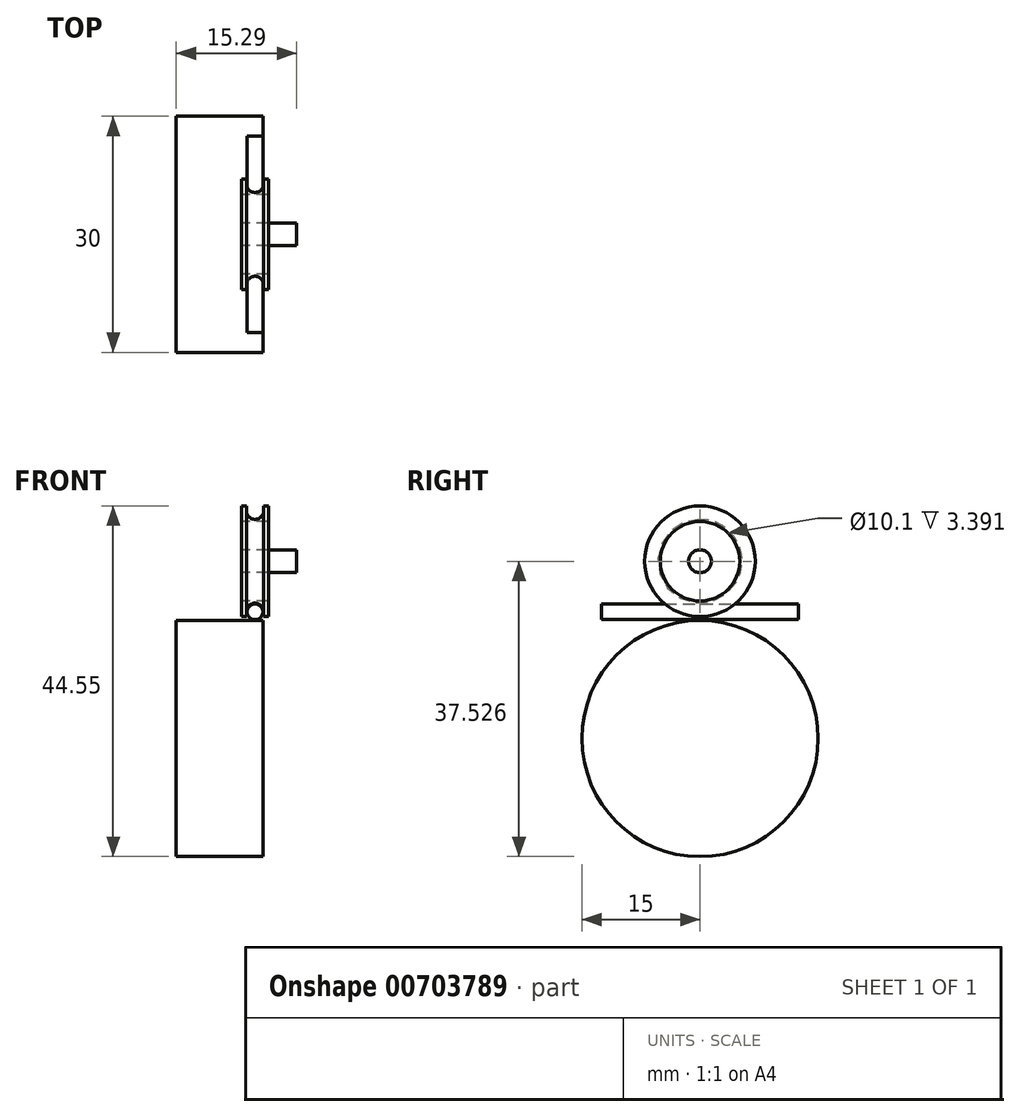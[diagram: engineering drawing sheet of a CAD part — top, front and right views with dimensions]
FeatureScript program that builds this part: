
annotation { "Feature Type Name" : "Feature", "Feature Type Description" : "" }
export const myFeature = defineFeature(function(context is Context, id is Id, definition is map)
    precondition{}
    {
        {
            var Q0;
            Q0=qCreatedBy(makeId("Front.planeOp"),FACE);
            var sketch = newSketch(context, id + "F0", { "sketchPlane" : qUnion([Q0])});
            skCircle(sketch, "E0", {"center": v(0, 0) * mm, "radius": 1 * mm, "construction": true});
            skLineSegment(sketch, "E1", {"start": v(0, 1) * mm, "end": v(4.5, 1) * mm, "construction": true});
            skLineSegment(sketch, "E2", {"start": v(0, -1) * mm, "end": v(4.5, -1) * mm, "construction": true});
            skLineSegment(sketch, "E3", {"start": v(0, 0) * mm, "end": v(4.5, 0) * mm, "construction": true});
            skCircle(sketch, "E4", {"center": v(4.5, 0) * mm, "radius": 1 * mm, "construction": true});
            skCircle(sketch, "E5.MirrorC", {"center": v(-4.5, 0) * mm, "radius": 1 * mm, "construction": true});
            skLineSegment(sketch, "E6.MirrorCS", {"start": v(0, 0) * mm, "end": v(-4.5, 0) * mm, "construction": true});
            skLineSegment(sketch, "E7.MirrorCS", {"start": v(0, -1) * mm, "end": v(-4.5, -1) * mm, "construction": true});
            skLineSegment(sketch, "E8.MirrorCS", {"start": v(0, 1) * mm, "end": v(-4.5, 1) * mm, "construction": true});
            skLineSegment(sketch, "E9", {"start": v(1, 0) * mm, "end": v(1, 10.9) * mm, "construction": true});
            skLineSegment(sketch, "E10", {"start": v(-1, 0) * mm, "end": v(-1, 10.9) * mm, "construction": true});
            skPoint(sketch, "E11", {"position": v(-5.5, 0) * mm});
            skPoint(sketch, "E12", {"position": v(5.5, 0) * mm});
            skPoint(sketch, "E13", {"position": v(-3.5, 0) * mm});
            skPoint(sketch, "E14", {"position": v(3.5, 0) * mm});
            skLineSegment(sketch, "E15.bottom", {"start": v(-5.33, -38) * mm, "end": v(-40.33, -38) * mm});
            skLineSegment(sketch, "E15.top", {"start": v(-5.33, -28.5) * mm, "end": v(-40.33, -28.5) * mm});
            skLineSegment(sketch, "E15.left", {"start": v(-5.33, -38) * mm, "end": v(-5.33, -28.5) * mm});
            skLineSegment(sketch, "E15.right", {"start": v(-40.33, -38) * mm, "end": v(-40.33, -28.5) * mm});
            skPoint(sketch, "E15.middle", {"position": v(-22.83, -33.26) * mm});
            skSolve(sketch);
        }
        {
            var Q0;
            Q0=qCreatedBy(makeId("Front.planeOp"),FACE);
            var sketch = newSketch(context, id + "F1", { "sketchPlane" : qUnion([Q0])});
            skCircle(sketch, "E16.0", {"center": v(-4.5, 0) * mm, "radius": 1 * mm, "construction": true});
            skCircle(sketch, "E16.1", {"center": v(0, 0) * mm, "radius": 1 * mm, "construction": true});
            skCircle(sketch, "E16.2", {"center": v(4.5, 0) * mm, "radius": 1 * mm, "construction": true});
            skLineSegment(sketch, "E16.3", {"start": v(0, 1) * mm, "end": v(4.5, 1) * mm, "construction": true});
            skLineSegment(sketch, "E16.4", {"start": v(0, -1) * mm, "end": v(4.5, -1) * mm, "construction": true});
            skLineSegment(sketch, "E16.5", {"start": v(0, -1) * mm, "end": v(-4.5, -1) * mm, "construction": true});
            skLineSegment(sketch, "E16.6", {"start": v(0, 1) * mm, "end": v(-4.5, 1) * mm, "construction": true});
            skLineSegment(sketch, "E16.7", {"start": v(1, 0) * mm, "end": v(1, 10.9) * mm, "construction": true});
            skLineSegment(sketch, "E16.8", {"start": v(-1, 0) * mm, "end": v(-1, 10.9) * mm, "construction": true});
            skLineSegment(sketch, "E17.bottom", {"start": v(-5.5, -1.1) * mm, "end": v(5.5, -1.1) * mm});
            skLineSegment(sketch, "E17.top", {"start": v(-5.5, -31.1) * mm, "end": v(5.5, -31.1) * mm});
            skLineSegment(sketch, "E17.left", {"start": v(-5.5, -1.1) * mm, "end": v(-5.5, -31.1) * mm});
            skLineSegment(sketch, "E17.right", {"start": v(5.5, -1.1) * mm, "end": v(5.5, -31.1) * mm});
            skPoint(sketch, "E17.middle", {"position": v(0, -16.1) * mm});
            skLineSegment(sketch, "E18.bottom", {"start": v(2.8, -0.6) * mm, "end": v(6.2, -0.6) * mm});
            skCircle(sketch, "E19.0", {"center": v(4.5, 0) * mm, "radius": 1.1 * mm});
            skLineSegment(sketch, "E20", {"start": v(3.4, 0) * mm, "end": v(3.4, -0.6) * mm});
            skLineSegment(sketch, "E21", {"start": v(5.6, 0) * mm, "end": v(5.6, -0.6) * mm});
            skLineSegment(sketch, "E22", {"start": v(2.8, 6.43) * mm, "end": v(6.2, 6.43) * mm});
            skLineSegment(sketch, "E23", {"start": v(6.2, -0.6) * mm, "end": v(6.2, 6.43) * mm});
            skLineSegment(sketch, "E24", {"start": v(2.8, -0.6) * mm, "end": v(2.8, 6.43) * mm});
            skLineSegment(sketch, "E25", {"start": v(4.5, 1.1) * mm, "end": v(4.5, 1.38) * mm, "construction": true});
            skLineSegment(sketch, "E26", {"start": v(4.5, 1.38) * mm, "end": v(2.8, 1.38) * mm});
            skLineSegment(sketch, "E27", {"start": v(4.5, 1.38) * mm, "end": v(6.2, 1.38) * mm});
            skLineSegment(sketch, "E28", {"start": v(2.8, 4.98) * mm, "end": v(6.2, 4.98) * mm});
            skLineSegment(sketch, "E29", {"start": v(6.2, 4.98) * mm, "end": v(9.79, 4.98) * mm});
            skLineSegment(sketch, "E30", {"start": v(6.2, 6.43) * mm, "end": v(9.79, 6.43) * mm});
            skLineSegment(sketch, "E31", {"start": v(9.79, 6.43) * mm, "end": v(9.79, 4.98) * mm});
            skLineSegment(sketch, "E32", {"start": v(-5.5, -16.1) * mm, "end": v(5.5, -16.1) * mm});
            skPoint(sketch, "E33.middle", {"position": v(5.5, -16.1) * mm});
            skLineSegment(sketch, "E34", {"start": v(6.2, 6.43) * mm, "end": v(6.2, 7.88) * mm});
            skLineSegment(sketch, "E35", {"start": v(6.2, 7.88) * mm, "end": v(9.79, 7.88) * mm});
            skLineSegment(sketch, "E36", {"start": v(9.79, 7.88) * mm, "end": v(9.79, 6.43) * mm});
            skLineSegment(sketch, "E37", {"start": v(6.8, 4.98) * mm, "end": v(6.8, -1.17) * mm});
            skLineSegment(sketch, "E38", {"start": v(9.79, 4.98) * mm, "end": v(9.79, -6.04) * mm});
            skLineSegment(sketch, "E39", {"start": v(5.6, 0) * mm, "end": v(6.2, 0) * mm, "construction": true});
            skLineSegment(sketch, "E40", {"start": v(3.4, 0) * mm, "end": v(2.8, 0) * mm, "construction": true});
            skLineSegment(sketch, "E41", {"start": v(5.5, -16.1) * mm, "end": v(6.5, -16.1) * mm});
            skLineSegment(sketch, "E42", {"start": v(6.5, -16.1) * mm, "end": v(12.2, -16.1) * mm});
            skLineSegment(sketch, "E43", {"start": v(12.2, -16.1) * mm, "end": v(12.2, -24.45) * mm});
            skLineSegment(sketch, "E44.MirrorCS", {"start": v(12.2, -16.1) * mm, "end": v(12.2, -7.75) * mm});
            skLineSegment(sketch, "E45", {"start": v(12.2, -7.75) * mm, "end": v(6.5, -7.75) * mm});
            skLineSegment(sketch, "E46", {"start": v(6.5, -7.75) * mm, "end": v(6.5, -16.1) * mm});
            skLineSegment(sketch, "E47", {"start": v(6.5, -16.1) * mm, "end": v(6.5, -24.45) * mm});
            skLineSegment(sketch, "E48", {"start": v(12.2, -24.45) * mm, "end": v(6.5, -24.45) * mm});
            skSolve(sketch);
        }
        {
            var Q0;
            Q0=qCreatedBy(makeId("Front.planeOp"),FACE);
            var sketch = newSketch(context, id + "F2", { "sketchPlane" : qUnion([Q0])});
            skCircle(sketch, "E49.0", {"center": v(-4.5, 0) * mm, "radius": 1 * mm});
            skCircle(sketch, "E49.1", {"center": v(4.5, 0) * mm, "radius": 1 * mm});
            skLineSegment(sketch, "E50", {"start": v(-4.5, -1) * mm, "end": v(4.5, -1) * mm, "construction": true});
            skLineSegment(sketch, "E51", {"start": v(4.5, -1) * mm, "end": v(6.6, -1) * mm, "construction": true});
            skLineSegment(sketch, "E52", {"start": v(-3.9, -1) * mm, "end": v(-4.5, -1) * mm, "construction": true});
            skLineSegment(sketch, "E53", {"start": v(-4.5, 1) * mm, "end": v(-4.5, -1) * mm, "construction": true});
            skLineSegment(sketch, "E54", {"start": v(-3.9, -1) * mm, "end": v(-3.9, -3) * mm, "construction": true});
            skLineSegment(sketch, "E55", {"start": v(-3.9, -3) * mm, "end": v(6.6, -3) * mm, "construction": true});
            skLineSegment(sketch, "E56", {"start": v(6.6, -3) * mm, "end": v(6.6, -1) * mm, "construction": true});
            skLineSegment(sketch, "E57", {"start": v(-4.68, 1.66) * mm, "end": v(-4.68, -0.66) * mm});
            skLineSegment(sketch, "E58", {"start": v(-4.68, -0.66) * mm, "end": v(-5.18, -0.66) * mm});
            skLineSegment(sketch, "E59", {"start": v(-5.18, -0.66) * mm, "end": v(-5.18, 2) * mm});
            skLineSegment(sketch, "E60", {"start": v(-2.68, 1.66) * mm, "end": v(-2.68, -0.66) * mm});
            skLineSegment(sketch, "E61", {"start": v(-2.68, -0.66) * mm, "end": v(-2.18, -0.66) * mm});
            skLineSegment(sketch, "E62", {"start": v(-2.18, -0.66) * mm, "end": v(-2.18, 2) * mm});
            skLineSegment(sketch, "E63", {"start": v(-5.5, 0) * mm, "end": v(-4.68, 0) * mm, "construction": true});
            skLineSegment(sketch, "E64", {"start": v(-2.68, 0) * mm, "end": v(-3.5, 0) * mm, "construction": true});
            skLineSegment(sketch, "E65", {"start": v(-4.68, -0.66) * mm, "end": v(-2.68, -0.66) * mm, "construction": true});
            skLineSegment(sketch, "E66.bottom", {"start": v(2.82, -0.72) * mm, "end": v(6.18, -0.72) * mm});
            skLineSegment(sketch, "E66.top", {"start": v(2.82, 1.74) * mm, "end": v(6.18, 1.74) * mm});
            skLineSegment(sketch, "E66.left", {"start": v(2.82, -0.72) * mm, "end": v(2.82, 1.74) * mm});
            skLineSegment(sketch, "E66.right", {"start": v(6.18, -0.72) * mm, "end": v(6.18, 1.74) * mm});
            skPoint(sketch, "E66.middle", {"position": v(4.5, 0.5) * mm});
            skLineSegment(sketch, "E67", {"start": v(3.5, 0) * mm, "end": v(3.5, -0.72) * mm});
            skLineSegment(sketch, "E68", {"start": v(5.5, 0) * mm, "end": v(5.5, -0.72) * mm});
            skLineSegment(sketch, "E69", {"start": v(1.38, 2.12) * mm, "end": v(5.95, 2.12) * mm, "construction": true});
            skCircle(sketch, "E70.0", {"center": v(4.5, 0) * mm, "radius": 1.1 * mm});
            skLineSegment(sketch, "E71", {"start": v(5.6, 0) * mm, "end": v(5.6, -0.72) * mm});
            skLineSegment(sketch, "E72", {"start": v(3.4, 0) * mm, "end": v(3.4, -0.72) * mm});
            skLineSegment(sketch, "E73.bottom", {"start": v(6.18, 1.74) * mm, "end": v(0, 1.74) * mm});
            skLineSegment(sketch, "E73.top", {"start": v(6.18, 2.12) * mm, "end": v(0, 2.12) * mm});
            skLineSegment(sketch, "E73.left", {"start": v(6.18, 1.74) * mm, "end": v(6.18, 2.12) * mm});
            skLineSegment(sketch, "E73.right", {"start": v(0, 1.74) * mm, "end": v(0, 2.12) * mm});
            skLineSegment(sketch, "E74.bottom", {"start": v(-1.22, 39.38) * mm, "end": v(8.78, 39.38) * mm});
            skLineSegment(sketch, "E74.top", {"start": v(-1.22, 13.38) * mm, "end": v(8.78, 13.38) * mm});
            skLineSegment(sketch, "E74.left", {"start": v(-1.22, 39.38) * mm, "end": v(-1.22, 13.38) * mm});
            skLineSegment(sketch, "E74.right", {"start": v(8.78, 39.38) * mm, "end": v(8.78, 13.38) * mm});
            skLineSegment(sketch, "E75.bottom", {"start": v(2.28, 3.38) * mm, "end": v(5.28, 3.38) * mm});
            skLineSegment(sketch, "E75.top", {"start": v(2.28, 23.38) * mm, "end": v(5.28, 23.38) * mm});
            skLineSegment(sketch, "E75.left", {"start": v(2.28, 3.38) * mm, "end": v(2.28, 23.38) * mm});
            skLineSegment(sketch, "E75.right", {"start": v(5.28, 3.38) * mm, "end": v(5.28, 23.38) * mm});
            skPoint(sketch, "E75.middle", {"position": v(3.78, 13.38) * mm});
            skSolve(sketch);
        }
        {
            var Q0;
            {var subQ0=sQuery(id+"F2.wireOp",EDGE,"E49.1");var subQ1=makeQuery(id+"F2.imprint","INTERSECT",VERTEX,{"derivedFrom":[subQ0,sQuery(id+"F2.wireOp",EDGE,"E67")]});Q0=makeQuery(id+"F2.imprint","IMPRINT",FACE,{"disambiguationData":[TD([[makeQuery(id+"F2.imprint","IMPRINT",EDGE,{"disambiguationData":[TD([[subQ1,1.0]])],"derivedFrom":subQ0}),1.0]])]});}
            var Q1;
            Q1=makeQuery(id+"F2.imprint","IMPRINT",FACE,{"disambiguationData":[TD([[makeQuery(id+"F2.imprint","IMPRINT",EDGE,{"derivedFrom":sQuery(id+"F2.wireOp",EDGE,"E49.0")}),-1.0]])]});
            var Q2;
            {var subQ0=sQuery(id+"F2.wireOp",EDGE,"E66.bottom");var subQ1=sQuery(id+"F2.wireOp",EDGE,"E49.1");var subQ2=makeQuery(id+"F2.imprint","INTERSECT",VERTEX,{"disambiguationData":[OD(0.0)],"derivedFrom":[subQ1,subQ0]});Q2=makeQuery(id+"F2.imprint","IMPRINT",FACE,{"disambiguationData":[TD([[makeQuery(id+"F2.imprint","IMPRINT",EDGE,{"disambiguationData":[TD([[subQ2,-1.0]])],"derivedFrom":subQ1}),1.0]])]});}
            extrude(context, id + "F3", {"entities" : qUnion([Q0, Q1, Q2]), "endBound" : BoundingType.SYMMETRIC, "depth" : 25 * mm, "offsetDistance" : 25 * mm});
        }
        {
            var Q0;
            {var subQ4=sQuery(id+"F1.wireOp",EDGE,"E20");Q0=makeQuery(id+"F1.imprint","IMPRINT",FACE,{"disambiguationData":[TD([[makeQuery(id+"F1.imprint","IMPRINT",EDGE,{"derivedFrom":subQ4}),-1.0]])]});}
            var Q1;
            {var subQ0=sQuery(id+"F1.wireOp",EDGE,"E22");Q1=makeQuery(id+"F1.imprint","IMPRINT",FACE,{"disambiguationData":[TD([[makeQuery(id+"F1.imprint","IMPRINT",EDGE,{"derivedFrom":subQ0}),-1.0]])]});}
            var Q2;
            {var subQ2=sQuery(id+"F1.wireOp",EDGE,"E29");Q2=makeQuery(id+"F1.imprint","IMPRINT",FACE,{"disambiguationData":[TD([[makeQuery(id+"F1.imprint","IMPRINT",EDGE,{"derivedFrom":subQ2}),1.0]])]});}
            var Q3;
            Q3=sQuery(id+"F1.wireOp",EDGE,"E22");
            revolve(context, id + "F4", {"surfaceOperationType" : NewSurfaceOperationType.NEW, "entities" : qUnion([Q0, Q1, Q2]), "axis" : qUnion([Q3]), "revolveType" : RevolveType.FULL});
        }
        {
            var Q0;
            {var subQ0=sQuery(id+"F1.wireOp",EDGE,"E17.left");var subQ1=sQuery(id+"F1.wireOp",EDGE,"E17.bottom");var subQ2=makeQuery(id+"F1.imprint","INTERSECT",VERTEX,{"derivedFrom":[subQ1,subQ0]});Q0=makeQuery(id+"F1.imprint","IMPRINT",FACE,{"disambiguationData":[TD([[makeQuery(id+"F1.imprint","IMPRINT",EDGE,{"disambiguationData":[TD([[subQ2,-1.0]])],"derivedFrom":subQ1}),-1.0]])]});}
            var Q1;
            {var subQ0=sQuery(id+"F1.wireOp",EDGE,"E32");var subQ1=sQuery(id+"F1.wireOp",EDGE,"E17.right");var subQ2=makeQuery(id+"F1.imprint","INTERSECT",VERTEX,{"derivedFrom":[subQ1,subQ0]});Q1=makeQuery(id+"F1.imprint","IMPRINT",FACE,{"disambiguationData":[TD([[makeQuery(id+"F1.imprint","IMPRINT",EDGE,{"disambiguationData":[TD([[subQ2,1.0]])],"derivedFrom":subQ1}),-1.0]])]});}
            var Q2;
            Q2=sQuery(id+"F1.wireOp",EDGE,"E32");
            revolve(context, id + "F5", {"surfaceOperationType" : NewSurfaceOperationType.NEW, "entities" : qUnion([Q0, Q1]), "axis" : qUnion([Q2]), "revolveType" : RevolveType.FULL});
        }
    });
